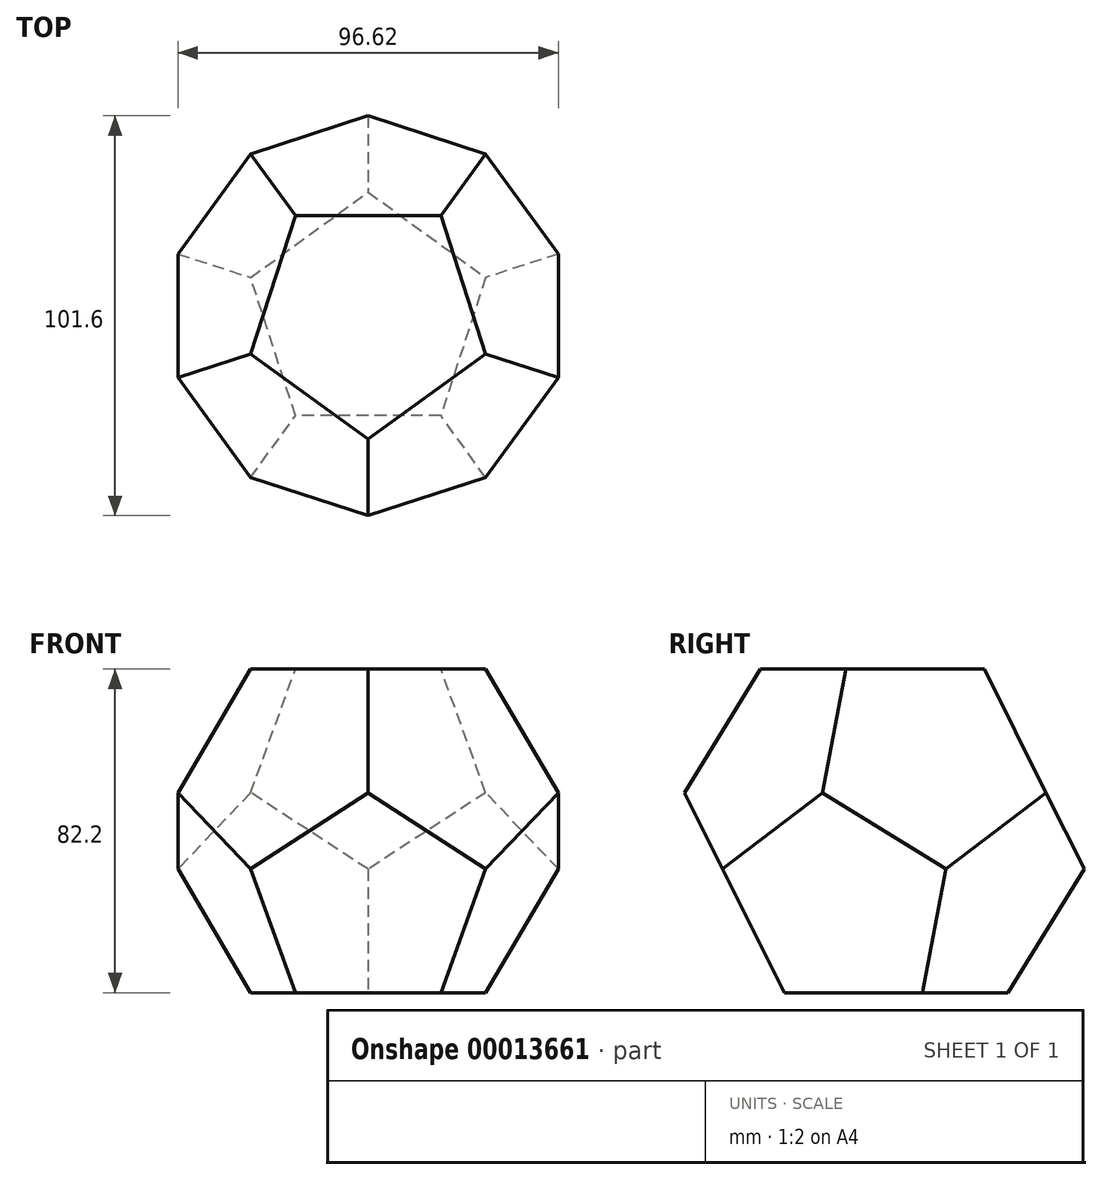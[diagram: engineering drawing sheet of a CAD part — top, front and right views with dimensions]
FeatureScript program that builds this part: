
annotation { "Feature Type Name" : "Feature", "Feature Type Description" : "" }
export const myFeature = defineFeature(function(context is Context, id is Id, definition is map)
    precondition{}
    {
        {
            var Q0;
            Q0=qCreatedBy(makeId("Right.planeOp"),FACE);
            var sketch = newSketch(context, id + "F0", { "sketchPlane" : qUnion([Q0])});
            skLineSegment(sketch, "E0.0", {"start": v(0, 133) * mm, "end": v(-82.2, 0) * mm});
            skPoint(sketch, "E1.orphan", {"position": v(-50.8, 50.8) * mm});
            skPoint(sketch, "E2.orphan", {"position": v(-31.4, 82.2) * mm});
            skLineSegment(sketch, "E3", {"start": v(0, 82.2) * mm, "end": v(0, 0) * mm});
            skLineSegment(sketch, "E4", {"start": v(0, 41.1) * mm, "end": v(84.2, 41.1) * mm});
            skSolve(sketch);
        }
        {
            var Q0;
            Q0=qCreatedBy(makeId("Top.planeOp"),FACE);
            var sketch = newSketch(context, id + "F1", { "sketchPlane" : qUnion([Q0])});
            skCircle(sketch, "E5.cCircle", {"center": v(0, 0) * mm, "radius": 66.5 * mm, "construction": true});
            skLineSegment(sketch, "E5.0", {"start": v(78.17, -25.4) * mm, "end": v(0, -82.2) * mm});
            skLineSegment(sketch, "E5.1", {"start": v(0, -82.2) * mm, "end": v(-78.17, -25.4) * mm});
            skLineSegment(sketch, "E5.2", {"start": v(-78.17, -25.4) * mm, "end": v(-48.31, 66.5) * mm});
            skLineSegment(sketch, "E5.3", {"start": v(-48.31, 66.5) * mm, "end": v(48.31, 66.5) * mm});
            skLineSegment(sketch, "E5.4", {"start": v(48.31, 66.5) * mm, "end": v(78.17, -25.4) * mm});
            skPoint(sketch, "E5.0.midPoint", {"position": v(39.09, -53.8) * mm});
            skSolve(sketch);
        }
        {
            var Q1;
            Q1=qSketchRegion(id+"F1",true);
            var Q2;
            Q2=sQuery(id+"F0.wireOp",VERTEX,"E0.0.start");
            loft(context, id + "F2", {"sheetProfilesArray" : [{ "sheetProfileEntities" : qUnion([Q1]) }, { "sheetProfileEntities" : qUnion([Q2]) }]});
        }
        {
            var Q0;
            Q0=makeQuery(id+"F2.opLoft","SWEPT_BODY",BODY,{"disambiguationData":[OSD([makeQuery(id+"F1.imprint","IMPRINT",FACE,{"disambiguationData":[TD([[makeQuery(id+"F1.imprint","IMPRINT",EDGE,{"derivedFrom":sQuery(id+"F1.wireOp",EDGE,"E5.0")}),-1.0]])]})])]});
            var Q1;
            Q1=sQuery(id+"F0.wireOp",EDGE,"E4");
            transform(context, id + "F3", {"entities" : qUnion([Q0]), "transformType" : TransformType.ROTATION, "transformAxis" : qUnion([Q1]), "angle" : 180 * degree, "makeCopy" : true});
        }
        {
            var Q0;
            Q0=makeQuery(id+"F3.opPattern","COPY",BODY,{"derivedFrom":makeQuery(id+"F2.opLoft","SWEPT_BODY",BODY,{"disambiguationData":[OSD([makeQuery(id+"F1.imprint","IMPRINT",FACE,{"disambiguationData":[TD([[makeQuery(id+"F1.imprint","IMPRINT",EDGE,{"derivedFrom":sQuery(id+"F1.wireOp",EDGE,"E5.0")}),-1.0]])]})])]}),"instanceName":"1"});
            var Q1;
            Q1=sQuery(id+"F0.wireOp",EDGE,"E3");
            transform(context, id + "F4", {"entities" : qUnion([Q0]), "transformType" : TransformType.ROTATION, "transformAxis" : qUnion([Q1]), "angle" : 36 * degree, "makeCopy" : false});
        }
        {
            var Q0;
            Q0=makeQuery(id+"F2.opLoft","SWEPT_BODY",BODY,{"disambiguationData":[OSD([makeQuery(id+"F1.imprint","IMPRINT",FACE,{"disambiguationData":[TD([[makeQuery(id+"F1.imprint","IMPRINT",EDGE,{"derivedFrom":sQuery(id+"F1.wireOp",EDGE,"E5.0")}),-1.0]])]})])]});
            var Q1;
            Q1=makeQuery(id+"F3.opPattern","COPY",BODY,{"derivedFrom":makeQuery(id+"F2.opLoft","SWEPT_BODY",BODY,{"disambiguationData":[OSD([makeQuery(id+"F1.imprint","IMPRINT",FACE,{"disambiguationData":[TD([[makeQuery(id+"F1.imprint","IMPRINT",EDGE,{"derivedFrom":sQuery(id+"F1.wireOp",EDGE,"E5.0")}),-1.0]])]})])]}),"instanceName":"1"});
            booleanBodies(context, id + "F5", {"operationType" : BooleanOperationType.INTERSECTION, "tools" : qUnion([Q0, Q1])});
        }
    });
